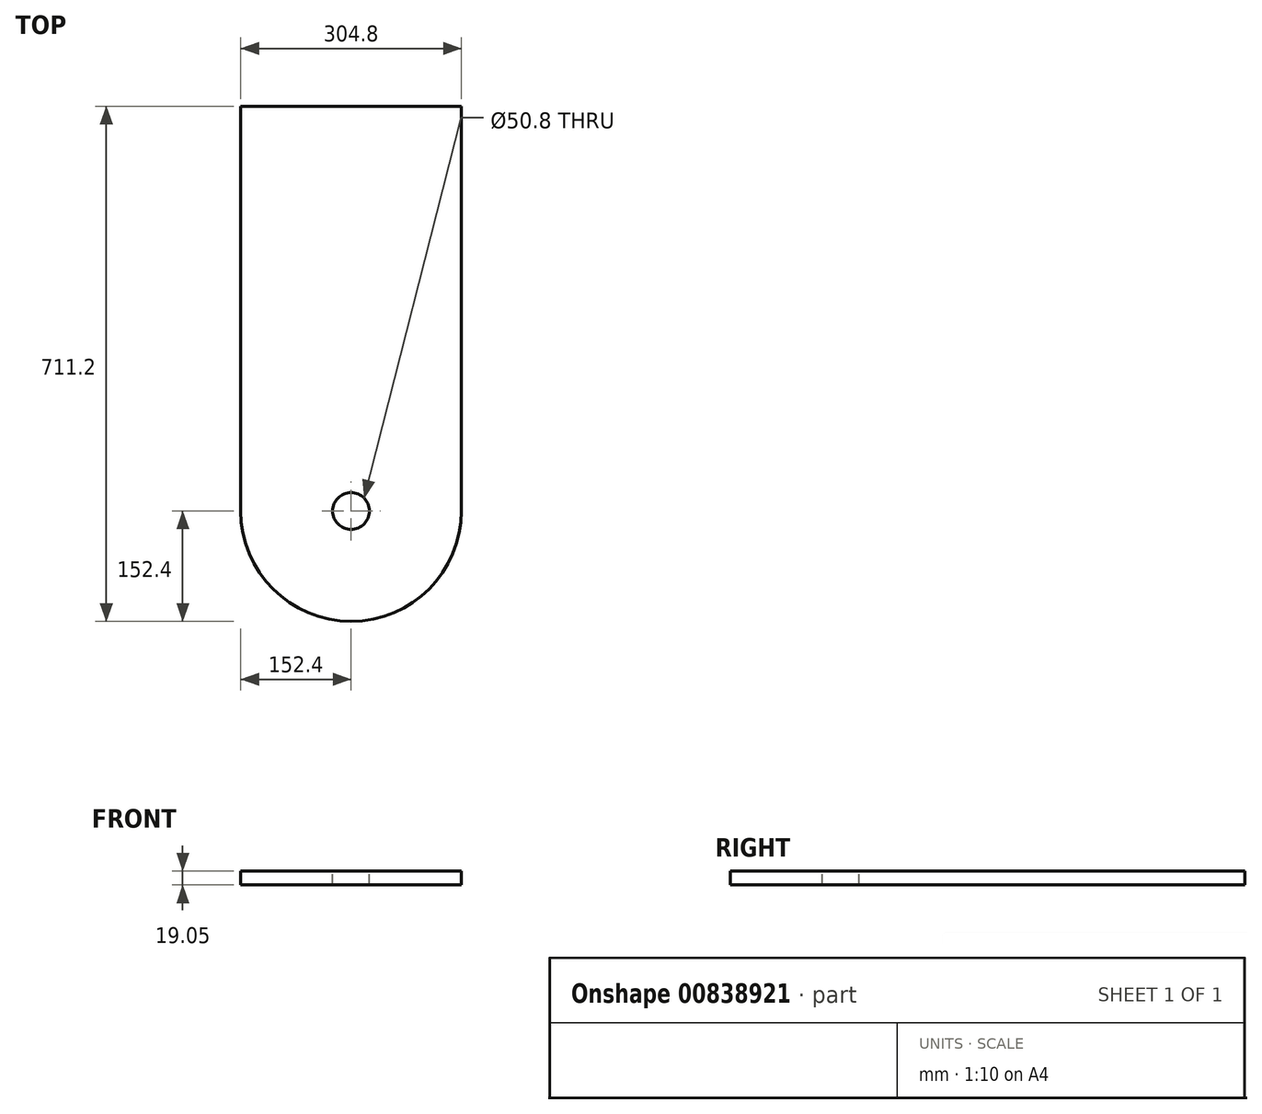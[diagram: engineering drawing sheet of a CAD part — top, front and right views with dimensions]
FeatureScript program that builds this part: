
annotation { "Feature Type Name" : "Feature", "Feature Type Description" : "" }
export const myFeature = defineFeature(function(context is Context, id is Id, definition is map)
    precondition{}
    {
        {
            var Q0;
            Q0=qCreatedBy(makeId("Top.planeOp"),FACE);
            var sketch = newSketch(context, id + "F0", { "sketchPlane" : qUnion([Q0])});
            skLineSegment(sketch, "E0", {"start": v(0, 711.2) * mm, "end": v(304.8, 711.2) * mm});
            skLineSegment(sketch, "E1", {"start": v(304.8, 711.2) * mm, "end": v(304.8, 152.4) * mm});
            skLineSegment(sketch, "E2", {"start": v(0, 711.2) * mm, "end": v(0, 152.4) * mm});
            skArc(sketch, "E3", {"start": v(0, 152.4) * mm, "mid": v(152.4, 0) * mm, "end": v(304.8, 152.4) * mm});
            skPoint(sketch, "E4.start.orphan", {"position": v(152.4, 0) * mm});
            skPoint(sketch, "E5.orphan", {"position": v(0, 0) * mm});
            skSolve(sketch);
        }
        {
            var Q0;
            Q0 = qSketchRegion(id + "F0", true);
            extrude(context, id + "F1", {"entities" : qUnion([Q0]), "depth" : 19.05 * mm, "offsetDistance" : 25.4 * mm});
        }
        {
            var Q0;
            Q0=makeQuery(id+"F1.opExtrude","CAP_FACE",FACE,{"disambiguationData":[OSD([sQuery(id+"F0.wireOp",EDGE,"E0"),sQuery(id+"F0.wireOp",EDGE,"E1"),sQuery(id+"F0.wireOp",EDGE,"E2"),sQuery(id+"F0.wireOp",EDGE,"E3")])],"isStart":false});
            var sketch = newSketch(context, id + "F2", { "sketchPlane" : qUnion([Q0])});
            skCircle(sketch, "E6", {"center": v(152.4, 152.4) * mm, "radius": 25.4 * mm});
            skSolve(sketch);
        }
        {
            var Q0;
            Q0 = qSketchRegion(id + "F2", true);
            extrude(context, id + "F3", {"entities" : qUnion([Q0]), "operationType" : NewBodyOperationType.REMOVE, "oppositeDirection" : true, "depth" : 78.74 * mm, "offsetDistance" : 25.4 * mm});
        }
    });
